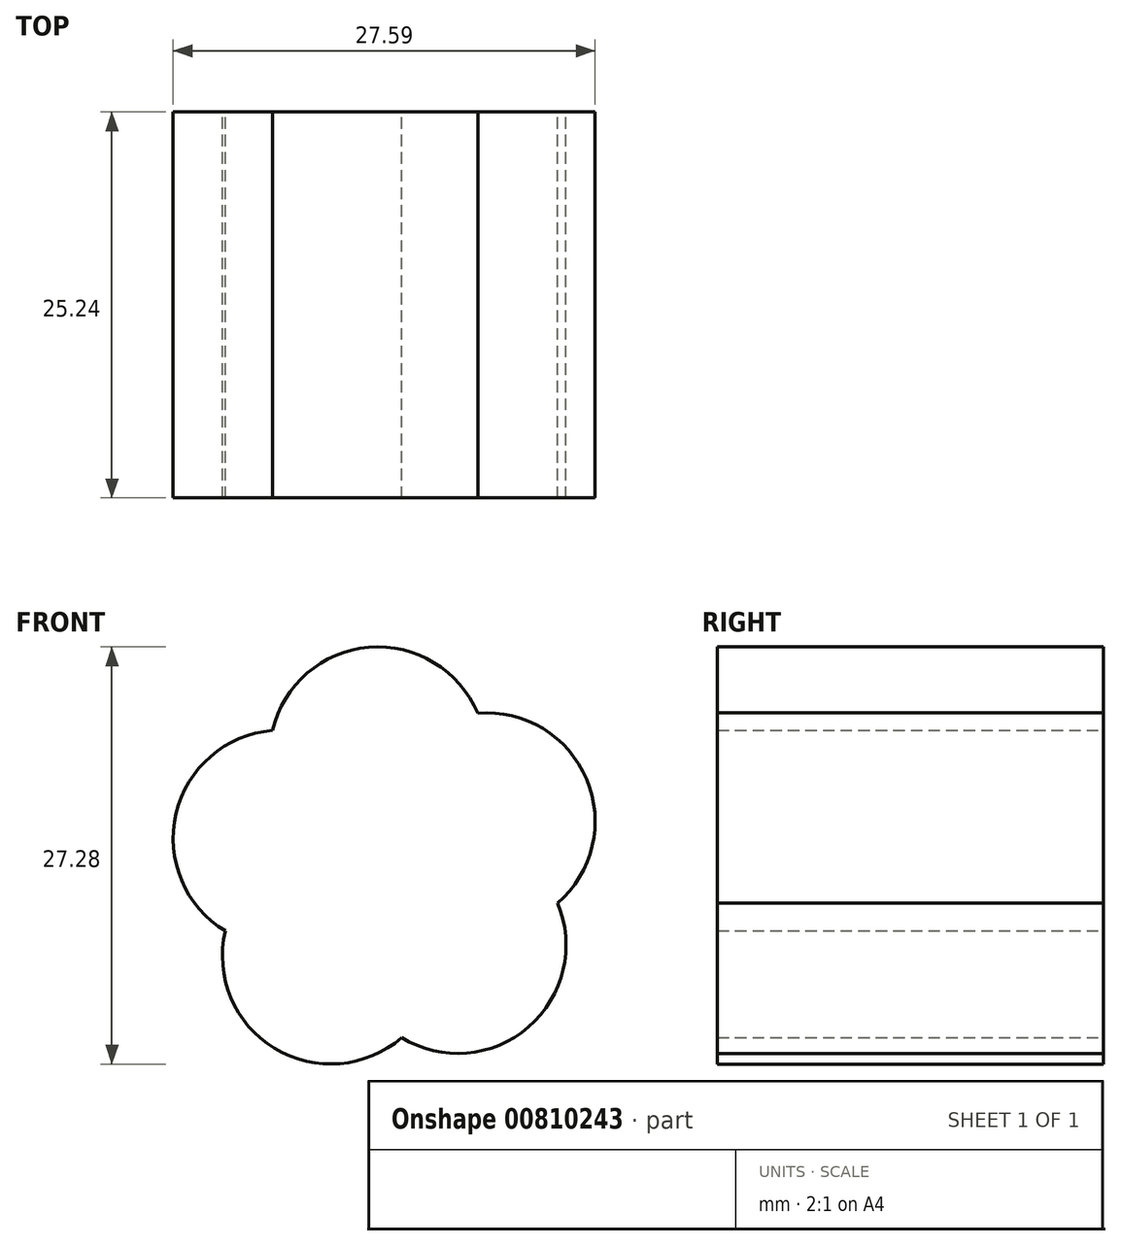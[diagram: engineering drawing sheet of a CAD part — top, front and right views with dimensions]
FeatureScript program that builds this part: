
annotation { "Feature Type Name" : "Feature", "Feature Type Description" : "" }
export const myFeature = defineFeature(function(context is Context, id is Id, definition is map)
    precondition{}
    {
        {
            var Q0;
            Q0=qCreatedBy(makeId("Top.planeOp"),FACE);
            var sketch = newSketch(context, id + "F0", { "sketchPlane" : qUnion([Q0])});
            skLineSegment(sketch, "E0.bottom", {"start": v(0, 0) * mm, "end": v(70.87, 0) * mm});
            skLineSegment(sketch, "E0.top", {"start": v(0, 25.24) * mm, "end": v(70.87, 25.24) * mm});
            skLineSegment(sketch, "E0.left", {"start": v(0, 0) * mm, "end": v(0, 25.24) * mm});
            skLineSegment(sketch, "E0.right", {"start": v(70.87, 0) * mm, "end": v(70.87, 25.24) * mm});
            skSolve(sketch);
        }
        {
            var Q0;
            Q0=makeQuery(id+"F0.imprint","IMPRINT",FACE,{"disambiguationData":[TD([[makeQuery(id+"F0.imprint","IMPRINT",EDGE,{"derivedFrom":sQuery(id+"F0.wireOp",EDGE,"E0.bottom")}),1.0]])]});
            extrude(context, id + "F1", {"entities" : qUnion([Q0]), "depth" : 63.8 * mm, "offsetDistance" : 25 * mm});
        }
        {
            var Q0;
            Q0=makeQuery(id+"F1.opExtrude","SWEPT_FACE",FACE,{"disambiguationData":[OSD([sQuery(id+"F0.wireOp",EDGE,"E0.top")])]});
            var sketch = newSketch(context, id + "F2", { "sketchPlane" : qUnion([Q0])});
            skCircle(sketch, "E1", {"center": v(-37.86, 39.02) * mm, "radius": 7.08 * mm});
            skCircle(sketch, "E2.1.0", {"center": v(-44.98, 34.7) * mm, "radius": 7.08 * mm});
            skCircle(sketch, "E2.2.0", {"center": v(-43.07, 26.6) * mm, "radius": 7.08 * mm});
            skPoint(sketch, "E2.center", {"position": v(-38.45, 31.96) * mm});
            skCircle(sketch, "E3.1.3.0", {"center": v(-34.78, 25.9) * mm, "radius": 7.08 * mm});
            skCircle(sketch, "E3.1.4.0", {"center": v(-31.55, 33.58) * mm, "radius": 7.08 * mm});
            skSolve(sketch);
        }
        {
            var Q0;
            {var subQ5=sQuery(id+"F0.wireOp",EDGE,"E0.top");Q0=makeQuery(id+"F2.imprint","IMPRINT",FACE,{"disambiguationData":[TD([[makeQuery(id+"F2.imprint","IMPRINT",EDGE,{"derivedFrom":makeQuery(id+"F1.opExtrude","CAP_EDGE",EDGE,{"disambiguationData":[OSD([subQ5])],"isStart":true})}),-1.0]])]});}
            extrude(context, id + "F3", {"entities" : qUnion([Q0]), "operationType" : NewBodyOperationType.REMOVE, "oppositeDirection" : true, "depth" : 93.9 * mm, "offsetDistance" : 25 * mm});
        }
    });
